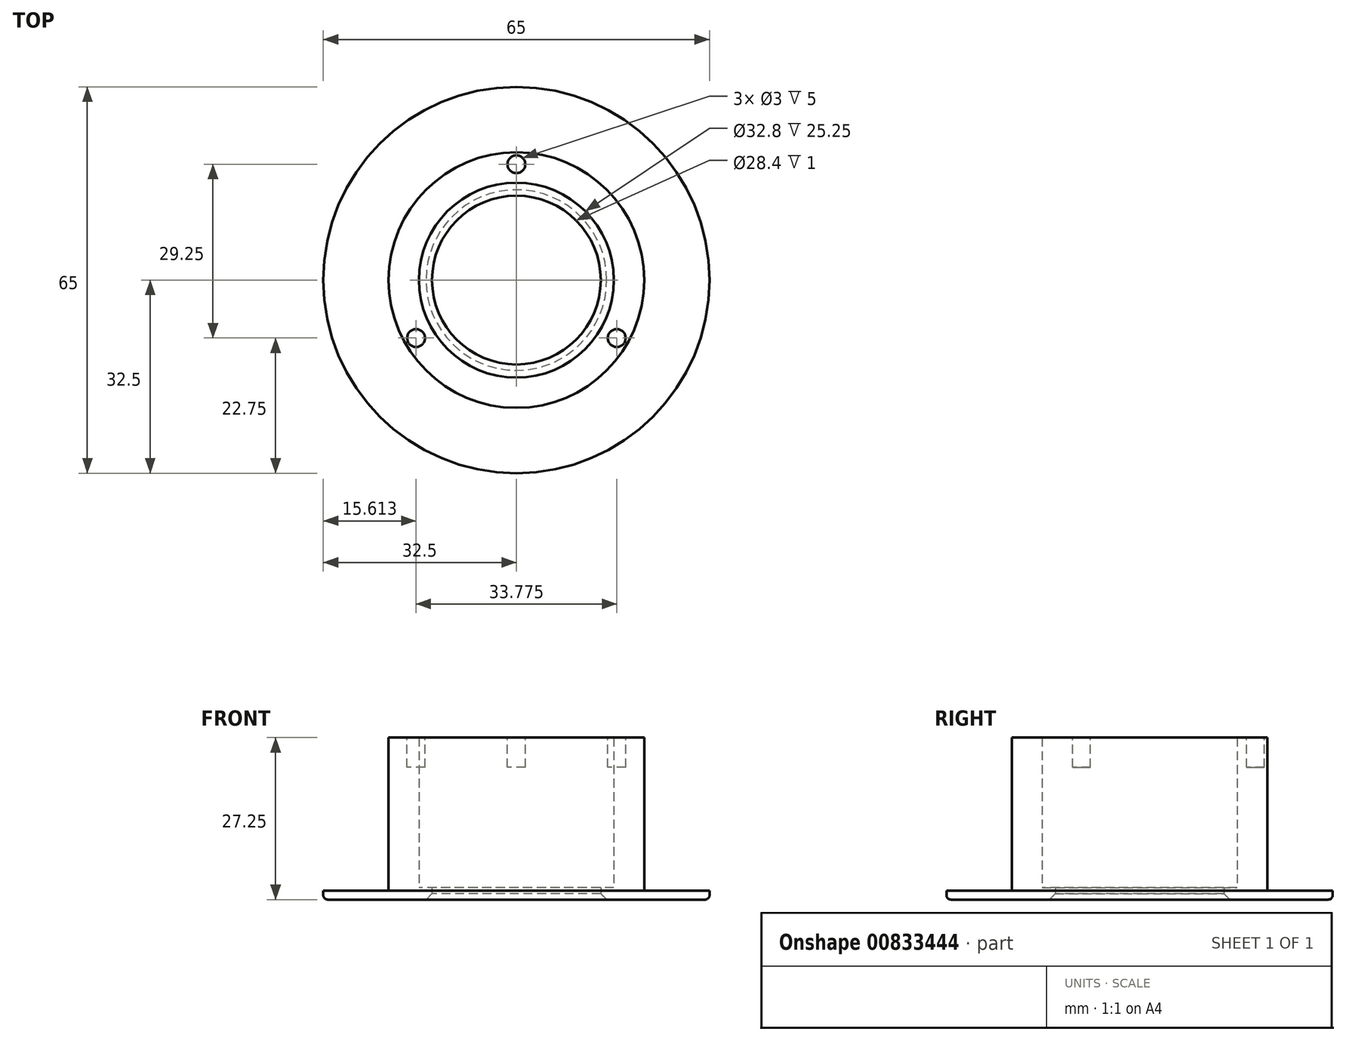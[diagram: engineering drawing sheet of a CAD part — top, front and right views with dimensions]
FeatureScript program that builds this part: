
annotation { "Feature Type Name" : "Feature", "Feature Type Description" : "" }
export const myFeature = defineFeature(function(context is Context, id is Id, definition is map)
    precondition{}
    {
        {
            var Q0;
            Q0=qCreatedBy(makeId("Top.planeOp"),FACE);
            var sketch = newSketch(context, id + "F0", { "sketchPlane" : qUnion([Q0])});
            skCircle(sketch, "E0", {"center": v(0, 0) * mm, "radius": 16.4 * mm});
            skCircle(sketch, "E1", {"center": v(0, 0) * mm, "radius": 21.5 * mm});
            skCircle(sketch, "E2", {"center": v(0, 0) * mm, "radius": 32.5 * mm});
            skCircle(sketch, "E3", {"center": v(0, 0) * mm, "radius": 14.2 * mm});
            skSolve(sketch);
        }
        {
            var Q0;
            Q0=makeQuery(id+"F0.imprint","IMPRINT",FACE,{"disambiguationData":[TD([[makeQuery(id+"F0.imprint","IMPRINT",EDGE,{"derivedFrom":sQuery(id+"F0.wireOp",EDGE,"E0")}),-1.0]])]});
            extrude(context, id + "F1", {"entities" : qUnion([Q0]), "depth" : 27.25 * mm, "offsetDistance" : 25 * mm});
        }
        {
            var Q0;
            Q0=makeQuery(id+"F0.imprint","IMPRINT",FACE,{"disambiguationData":[TD([[makeQuery(id+"F0.imprint","IMPRINT",EDGE,{"derivedFrom":sQuery(id+"F0.wireOp",EDGE,"E1")}),-1.0]])]});
            extrude(context, id + "F2", {"entities" : qUnion([Q0]), "operationType" : NewBodyOperationType.ADD, "depth" : 1.5 * mm, "offsetDistance" : 25 * mm});
        }
        {
            var Q0;
            Q0=makeQuery(id+"F0.imprint","IMPRINT",FACE,{"disambiguationData":[TD([[makeQuery(id+"F0.imprint","IMPRINT",EDGE,{"derivedFrom":sQuery(id+"F0.wireOp",EDGE,"E0")}),1.0]])]});
            extrude(context, id + "F3", {"entities" : qUnion([Q0]), "operationType" : NewBodyOperationType.ADD, "depth" : 1 * mm, "offsetDistance" : 25 * mm});
        }
        {
            var Q0;
            Q0=makeQuery(id+"F1.opExtrude","CAP_FACE",FACE,{"disambiguationData":[OSD([sQuery(id+"F0.wireOp",EDGE,"E0"),sQuery(id+"F0.wireOp",EDGE,"E1")])],"isStart":false});
            var sketch = newSketch(context, id + "F4", { "sketchPlane" : qUnion([Q0])});
            skCircle(sketch, "E4", {"center": v(0, 0) * mm, "radius": 19.5 * mm});
            skCircle(sketch, "E5", {"center": v(0, 19.5) * mm, "radius": 1.5 * mm});
            skCircle(sketch, "E6.1.0", {"center": v(-16.89, -9.75) * mm, "radius": 1.5 * mm});
            skCircle(sketch, "E6.2.0", {"center": v(16.89, -9.75) * mm, "radius": 1.5 * mm});
            skSolve(sketch);
        }
        {
            var Q0;
            {var subQ0=sQuery(id+"F4.wireOp",EDGE,"E5");var subQ1=sQuery(id+"F4.wireOp",EDGE,"E4");var subQ2=makeQuery(id+"F4.imprint","INTERSECT",VERTEX,{"disambiguationData":[OD(0.0)],"derivedFrom":[subQ1,subQ0]});Q0=makeQuery(id+"F4.imprint","IMPRINT",FACE,{"disambiguationData":[TD([[makeQuery(id+"F4.imprint","IMPRINT",EDGE,{"disambiguationData":[TD([[subQ2,1.0]])],"derivedFrom":subQ1}),1.0]])]});}
            var Q1;
            {var subQ0=sQuery(id+"F4.wireOp",EDGE,"E5");var subQ1=sQuery(id+"F4.wireOp",EDGE,"E4");var subQ2=makeQuery(id+"F4.imprint","INTERSECT",VERTEX,{"disambiguationData":[OD(0.0)],"derivedFrom":[subQ1,subQ0]});Q1=makeQuery(id+"F4.imprint","IMPRINT",FACE,{"disambiguationData":[TD([[makeQuery(id+"F4.imprint","IMPRINT",EDGE,{"disambiguationData":[TD([[subQ2,1.0]])],"derivedFrom":subQ1}),-1.0]])]});}
            var Q2;
            {var subQ0=sQuery(id+"F4.wireOp",EDGE,"E6.2.0");var subQ1=sQuery(id+"F4.wireOp",EDGE,"E4");var subQ2=makeQuery(id+"F4.imprint","INTERSECT",VERTEX,{"disambiguationData":[OD(0.0)],"derivedFrom":[subQ1,subQ0]});Q2=makeQuery(id+"F4.imprint","IMPRINT",FACE,{"disambiguationData":[TD([[makeQuery(id+"F4.imprint","IMPRINT",EDGE,{"disambiguationData":[TD([[subQ2,-1.0]])],"derivedFrom":subQ1}),-1.0]])]});}
            var Q3;
            {var subQ0=sQuery(id+"F4.wireOp",EDGE,"E6.2.0");var subQ1=sQuery(id+"F4.wireOp",EDGE,"E4");var subQ2=makeQuery(id+"F4.imprint","INTERSECT",VERTEX,{"disambiguationData":[OD(0.0)],"derivedFrom":[subQ1,subQ0]});Q3=makeQuery(id+"F4.imprint","IMPRINT",FACE,{"disambiguationData":[TD([[makeQuery(id+"F4.imprint","IMPRINT",EDGE,{"disambiguationData":[TD([[subQ2,-1.0]])],"derivedFrom":subQ1}),1.0]])]});}
            var Q4;
            {var subQ0=sQuery(id+"F4.wireOp",EDGE,"E6.1.0");var subQ1=sQuery(id+"F4.wireOp",EDGE,"E4");var subQ2=makeQuery(id+"F4.imprint","INTERSECT",VERTEX,{"disambiguationData":[OD(0.0)],"derivedFrom":[subQ1,subQ0]});Q4=makeQuery(id+"F4.imprint","IMPRINT",FACE,{"disambiguationData":[TD([[makeQuery(id+"F4.imprint","IMPRINT",EDGE,{"disambiguationData":[TD([[subQ2,-1.0]])],"derivedFrom":subQ1}),1.0]])]});}
            var Q5;
            {var subQ0=sQuery(id+"F4.wireOp",EDGE,"E6.1.0");var subQ1=sQuery(id+"F4.wireOp",EDGE,"E4");var subQ2=makeQuery(id+"F4.imprint","INTERSECT",VERTEX,{"disambiguationData":[OD(0.0)],"derivedFrom":[subQ1,subQ0]});Q5=makeQuery(id+"F4.imprint","IMPRINT",FACE,{"disambiguationData":[TD([[makeQuery(id+"F4.imprint","IMPRINT",EDGE,{"disambiguationData":[TD([[subQ2,-1.0]])],"derivedFrom":subQ1}),-1.0]])]});}
            extrude(context, id + "F5", {"entities" : qUnion([Q0, Q1, Q2, Q3, Q4, Q5]), "operationType" : NewBodyOperationType.REMOVE, "oppositeDirection" : true, "depth" : 5 * mm, "offsetDistance" : 25 * mm});
        }
        {
            var Q0;
            Q0=makeQuery(id+"F2.opExtrude","CAP_EDGE",EDGE,{"disambiguationData":[OSD([sQuery(id+"F0.wireOp",EDGE,"E2")])],"isStart":true});
            fillet(context, id + "F6", {"entities" : qUnion([Q0]), "radius" : .75 * mm, "tangentPropagation" : true, "allowEdgeOverflow" : false});
        }
        {
            var Q0;
            Q0=makeQuery(id+"F3.opExtrude","CAP_EDGE",EDGE,{"disambiguationData":[OSD([sQuery(id+"F0.wireOp",EDGE,"E3")])],"isStart":true});
            chamfer(context, id + "F7", {"entities" : qUnion([Q0]), "width" : 1 * mm, "tangentPropagation" : true});
        }
        {
            var Q0;
            Q0=makeQuery(id+"F3.opExtrude","CAP_FACE",FACE,{"disambiguationData":[OSD([sQuery(id+"F0.wireOp",EDGE,"E0"),sQuery(id+"F0.wireOp",EDGE,"E3")])],"isStart":false});
            extrude(context, id + "F8", {"entities" : qUnion([Q0]), "operationType" : NewBodyOperationType.ADD, "depth" : 1 * mm, "offsetDistance" : 25 * mm});
        }
    });
